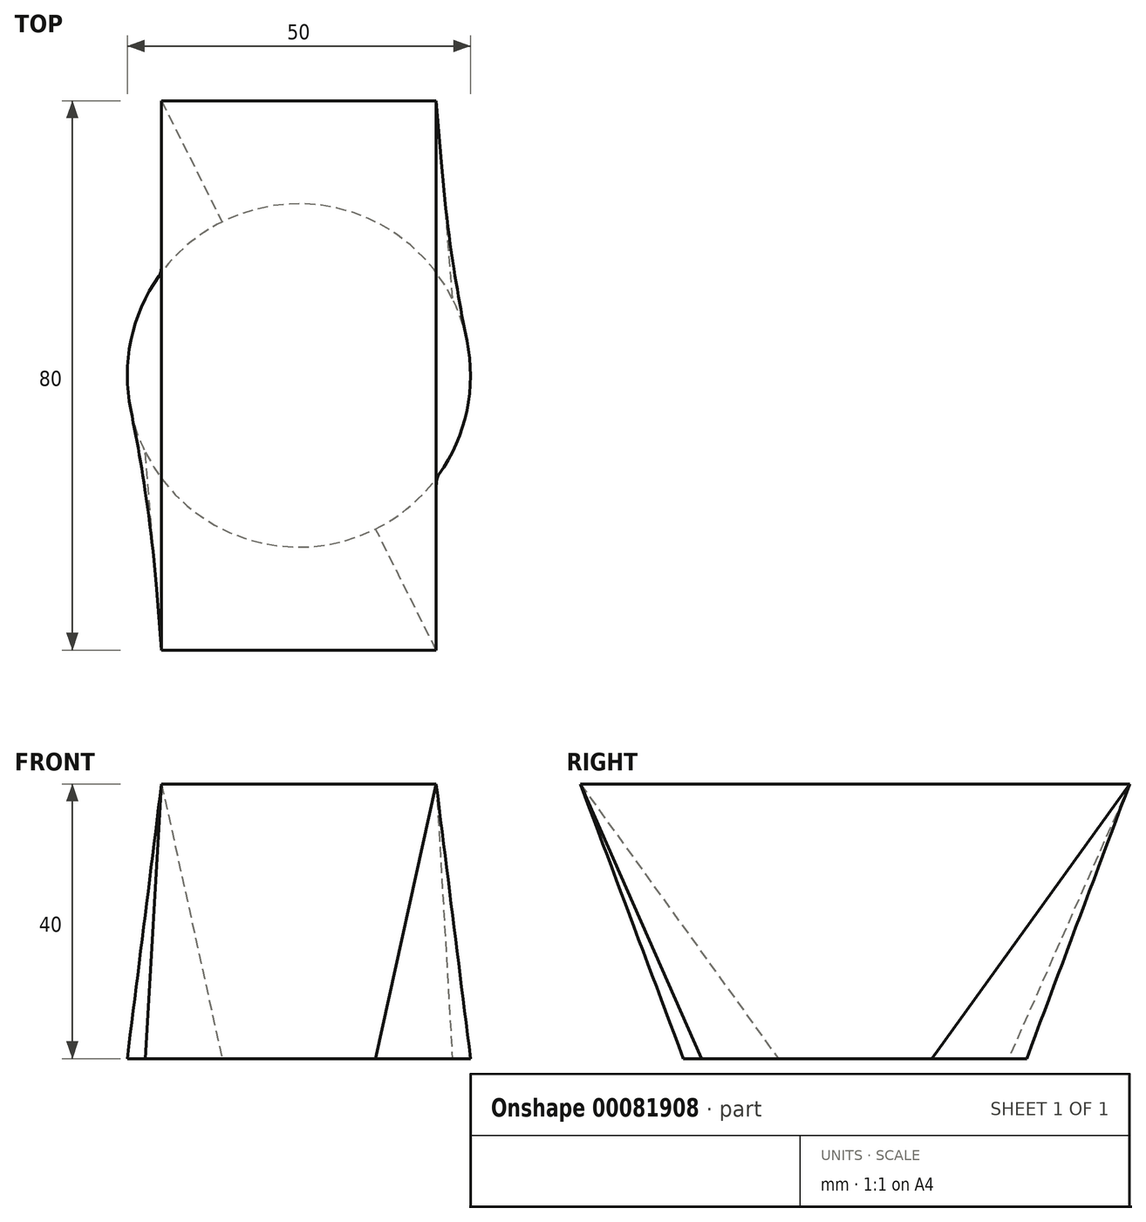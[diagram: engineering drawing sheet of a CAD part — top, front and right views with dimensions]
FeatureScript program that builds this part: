
annotation { "Feature Type Name" : "Feature", "Feature Type Description" : "" }
export const myFeature = defineFeature(function(context is Context, id is Id, definition is map)
    precondition{}
    {
        {
            var Q0;
            Q0=qCreatedBy(makeId("Top.planeOp"),FACE);
            var sketch = newSketch(context, id + "F0", { "sketchPlane" : qUnion([Q0])});
            skCircle(sketch, "E0", {"center": v(0, 0) * mm, "radius": 25 * mm});
            skPoint(sketch, "E1", {"position": v(-12.86, 21.44) * mm});
            skPoint(sketch, "E2", {"position": v(-17.54, -17.8) * mm});
            skPoint(sketch, "E3", {"position": v(15.2, -19.84) * mm});
            skPoint(sketch, "E4", {"position": v(14.8, 20.15) * mm});
            skSolve(sketch);
        }
        {
            var Q0;
            Q0=qCreatedBy(makeId("Top.planeOp"),FACE);
            cPlane(context, id + "F1", {"entities" : qUnion([Q0]), "cplaneType" : CPlaneType.OFFSET, "offset" : 40 * mm, "width" : 150 * mm, "height" : 150 * mm});
        }
        {
            var Q0;
            Q0=qCreatedBy(id+"F1.planeOp",FACE);
            var sketch = newSketch(context, id + "F2", { "sketchPlane" : qUnion([Q0])});
            skLineSegment(sketch, "E5.bottom", {"start": v(20, -40) * mm, "end": v(-20, -40) * mm});
            skLineSegment(sketch, "E5.top", {"start": v(20, 40) * mm, "end": v(-20, 40) * mm});
            skLineSegment(sketch, "E5.left", {"start": v(20, -40) * mm, "end": v(20, 40) * mm});
            skLineSegment(sketch, "E5.right", {"start": v(-20, -40) * mm, "end": v(-20, 40) * mm});
            skPoint(sketch, "E5.middle", {"position": v(0, 0) * mm});
            skSolve(sketch);
        }
        {
            var Q0;
            Q0=makeQuery(id+"F2.imprint","IMPRINT",FACE,{"disambiguationData":[TD([[makeQuery(id+"F2.imprint","IMPRINT",EDGE,{"derivedFrom":sQuery(id+"F2.wireOp",EDGE,"E5.bottom")}),-1.0]])]});
            var Q1;
            Q1=makeQuery(id+"F0.imprint","IMPRINT",FACE,{"disambiguationData":[TD([[makeQuery(id+"F0.imprint","IMPRINT",EDGE,{"derivedFrom":sQuery(id+"F0.wireOp",EDGE,"E0")}),1.0]])]});
            var Q2;
            Q2=sQuery(id+"F0.wireOp",VERTEX,"E4");
            var Q3;
            Q3=sQuery(id+"F2.wireOp",VERTEX,"E5.left.end");
            var Q4;
            Q4=sQuery(id+"F0.wireOp",VERTEX,"E1");
            var Q5;
            Q5=sQuery(id+"F2.wireOp",VERTEX,"E5.top.end");
            var Q6;
            Q6=sQuery(id+"F0.wireOp",VERTEX,"E2");
            var Q7;
            Q7=sQuery(id+"F2.wireOp",VERTEX,"E5.right.start");
            var Q8;
            Q8=sQuery(id+"F0.wireOp",VERTEX,"E3");
            var Q9;
            Q9=sQuery(id+"F2.wireOp",VERTEX,"E5.left.start");
            loft(context, id + "F3", {"sheetProfilesArray" : [{ "sheetProfileEntities" : qUnion([Q0]) }, { "sheetProfileEntities" : qUnion([Q1]) }], "connections" : [{ "connectionEntities" : qUnion([Q2, Q3, Q4, Q5, Q6, Q7, Q8, Q9]), "connectionEdgeQueries" : qUnion([]), "connectionEdgeParameters" : [] }]});
        }
    });
